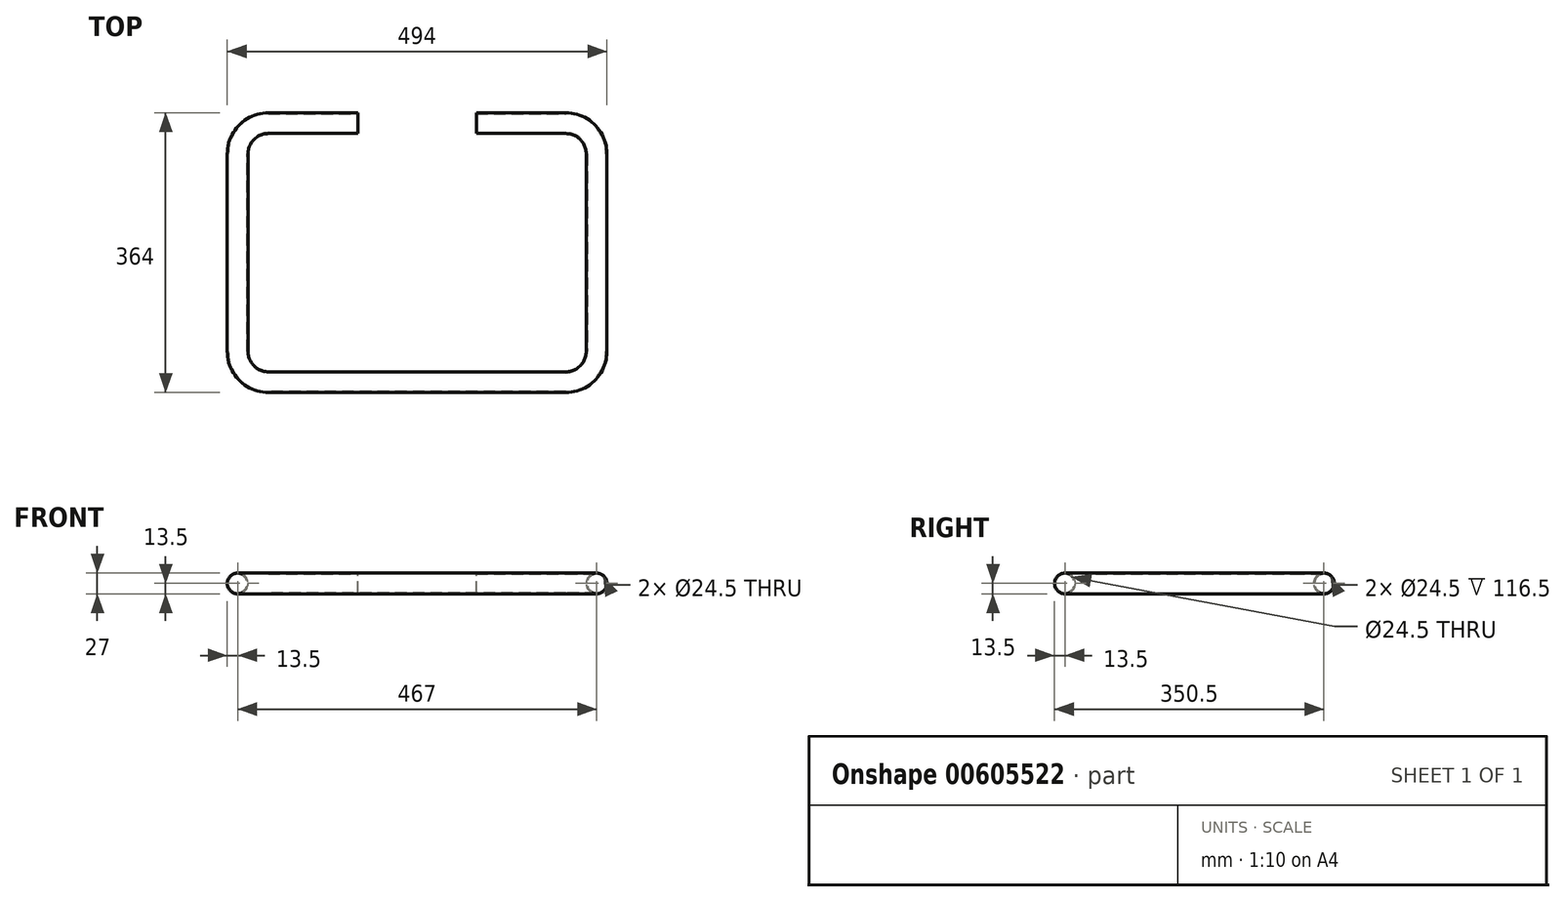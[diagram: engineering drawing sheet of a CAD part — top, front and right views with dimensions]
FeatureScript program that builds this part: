
annotation { "Feature Type Name" : "Feature", "Feature Type Description" : "" }
export const myFeature = defineFeature(function(context is Context, id is Id, definition is map)
    precondition{}
    {
        {
            var Q0;
            Q0=qCreatedBy(makeId("Right.planeOp"),FACE);
            var sketch = newSketch(context, id + "F0", { "sketchPlane" : qUnion([Q0])});
            skCircle(sketch, "E0", {"center": v(0, 0) * mm, "radius": 12.25 * mm});
            skCircle(sketch, "E1", {"center": v(0, 0) * mm, "radius": 13.5 * mm});
            skSolve(sketch);
        }
        {
            var Q0;
            Q0=qCreatedBy(makeId("Top.planeOp"),FACE);
            var sketch = newSketch(context, id + "F1", { "sketchPlane" : qUnion([Q0])});
            skLineSegment(sketch, "E2", {"start": v(0, 0) * mm, "end": v(116.5, 0) * mm});
            skLineSegment(sketch, "E3", {"start": v(156.5, -40) * mm, "end": v(156.5, -297) * mm});
            skLineSegment(sketch, "E4", {"start": v(116.5, -337) * mm, "end": v(-270.5, -337) * mm});
            skLineSegment(sketch, "E5", {"start": v(-310.5, -297) * mm, "end": v(-310.5, -40) * mm});
            skLineSegment(sketch, "E6", {"start": v(-270.5, 0) * mm, "end": v(-154, 0) * mm});
            skPoint(sketch, "E7.visualSharp", {"position": v(156.5, 0) * mm});
            skArc(sketch, "E7.filletArc", {"start": v(156.5, -40) * mm, "mid": v(144.78, -11.72) * mm, "end": v(116.5, 0) * mm});
            skPoint(sketch, "E8.visualSharp", {"position": v(156.5, -337) * mm});
            skArc(sketch, "E8.filletArc", {"start": v(116.5, -337) * mm, "mid": v(144.78, -325.28) * mm, "end": v(156.5, -297) * mm});
            skPoint(sketch, "E9.visualSharp", {"position": v(-310.5, -337) * mm});
            skArc(sketch, "E9.filletArc", {"start": v(-310.5, -297) * mm, "mid": v(-298.78, -325.28) * mm, "end": v(-270.5, -337) * mm});
            skPoint(sketch, "E10.visualSharp", {"position": v(-310.5, 0) * mm});
            skArc(sketch, "E10.filletArc", {"start": v(-270.5, 0) * mm, "mid": v(-298.78, -11.72) * mm, "end": v(-310.5, -40) * mm});
            skSolve(sketch);
        }
        {
            var Q0;
            Q0=makeQuery(id+"F0.imprint","IMPRINT",FACE,{"disambiguationData":[TD([[makeQuery(id+"F0.imprint","IMPRINT",EDGE,{"derivedFrom":sQuery(id+"F0.wireOp",EDGE,"E0")}),-1.0]])]});
            var Q1;
            Q1=sQuery(id+"F1.wireOp",EDGE,"E2");
            var Q2;
            Q2=sQuery(id+"F1.wireOp",EDGE,"E7.filletArc");
            var Q3;
            Q3=sQuery(id+"F1.wireOp",EDGE,"E3");
            var Q4;
            Q4=sQuery(id+"F1.wireOp",EDGE,"E8.filletArc");
            var Q5;
            Q5=sQuery(id+"F1.wireOp",EDGE,"E4");
            var Q6;
            Q6=sQuery(id+"F1.wireOp",EDGE,"E9.filletArc");
            var Q7;
            Q7=sQuery(id+"F1.wireOp",EDGE,"E5");
            var Q8;
            Q8=sQuery(id+"F1.wireOp",EDGE,"E10.filletArc");
            var Q9;
            Q9=sQuery(id+"F1.wireOp",EDGE,"E6");
            sweep(context, id + "F2", {"profiles" : qUnion([Q0]), "path" : qUnion([Q1, Q2, Q3, Q4, Q5, Q6, Q7, Q8, Q9])});
        }
    });
